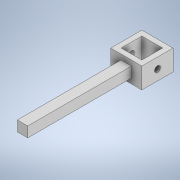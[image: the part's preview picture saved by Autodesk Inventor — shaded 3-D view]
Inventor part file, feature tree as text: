
AUTODESK INVENTOR PART (.ipt)
format: ipt  version: 2020.3 (Build 243373000, 373)  size: 131,584 bytes
history: native  units: mm
features: extrude x3, sketch x3
ambient origin geometry x8: Origin, YZ Plane, XZ Plane, XY Plane, X Axis, Y Axis, Z Axis, Center Point
bodies: Solid1 (feature_tree)
feature tree (6):
  extrude  "Extrusion1"  Depth=15.0mm
  extrude  "Extrusion2"  Depth=2.5mm
  extrude  "Extrusion3"  Depth=10.0mm
  sketch  "Sketch1"  dims[d0=15.0mm d1=15.0mm]
  sketch  "Sketch2"  dims[d2=2.5mm d3=2.5mm]
  sketch  "Sketch3"  dims[d4=10.0mm d5=10.0mm d6=10.0mm d7=0.0mm d8=7.5mm d9=5.0mm d10=2.8mm d11=0.0mm d12=0.0mm d13=5.0mm d14=2.5mm d15=5.0mm d16=5.0mm d17=50.0mm d18=0.0mm]
